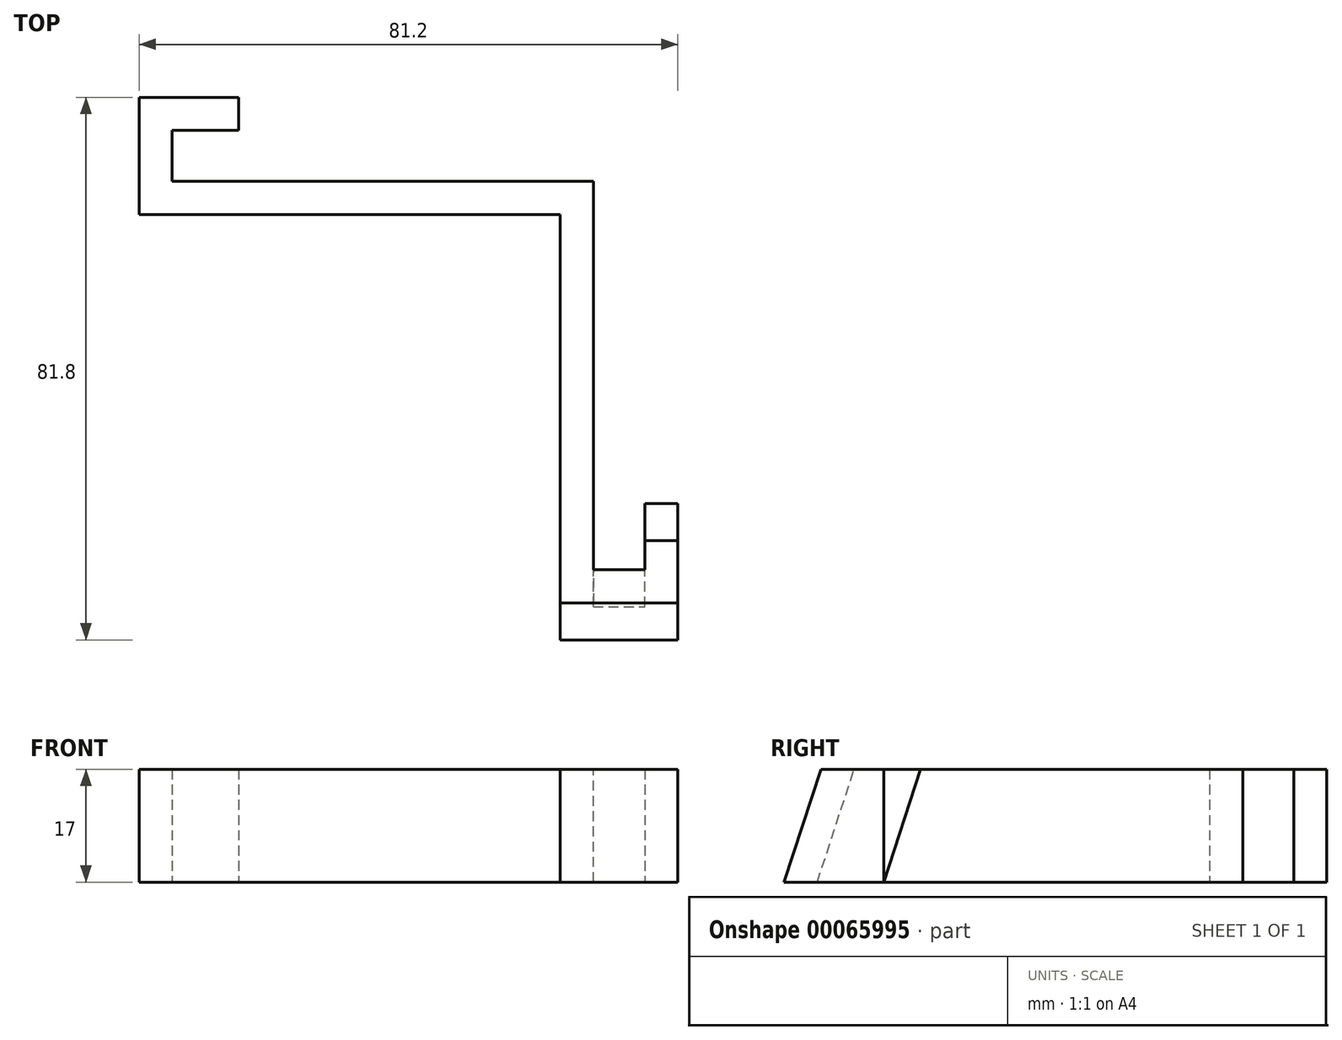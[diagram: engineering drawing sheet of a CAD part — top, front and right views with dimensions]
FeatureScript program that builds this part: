
annotation { "Feature Type Name" : "Feature", "Feature Type Description" : "" }
export const myFeature = defineFeature(function(context is Context, id is Id, definition is map)
    precondition{}
    {
        {
            var Q0;
            Q0=qCreatedBy(makeId("Top.planeOp"),FACE);
            var sketch = newSketch(context, id + "F0", { "sketchPlane" : qUnion([Q0])});
            skLineSegment(sketch, "E0", {"start": v(0, 0) * mm, "end": v(-63.45, 0) * mm});
            skLineSegment(sketch, "E1", {"start": v(0, 0) * mm, "end": v(0, -64.15) * mm});
            skLineSegment(sketch, "E2", {"start": v(0, -64.15) * mm, "end": v(7.75, -64.15) * mm});
            skLineSegment(sketch, "E3", {"start": v(-63.45, 0) * mm, "end": v(-63.45, 7.65) * mm});
            skLineSegment(sketch, "E4", {"start": v(7.75, -64.15) * mm, "end": v(7.75, -54.15) * mm});
            skLineSegment(sketch, "E5", {"start": v(7.75, -54.15) * mm, "end": v(12.75, -54.15) * mm});
            skLineSegment(sketch, "E6", {"start": v(-63.45, 7.65) * mm, "end": v(-53.45, 7.65) * mm});
            skLineSegment(sketch, "E7", {"start": v(-53.45, 7.65) * mm, "end": v(-53.45, 12.65) * mm});
            skLineSegment(sketch, "E8", {"start": v(12.75, -54.15) * mm, "end": v(12.75, -69.15) * mm});
            skLineSegment(sketch, "E9", {"start": v(12.75, -69.15) * mm, "end": v(-5, -69.15) * mm});
            skLineSegment(sketch, "E10", {"start": v(-5, -69.15) * mm, "end": v(-5, -5) * mm});
            skLineSegment(sketch, "E11", {"start": v(-5, -5) * mm, "end": v(-68.45, -5) * mm});
            skLineSegment(sketch, "E12", {"start": v(-68.45, -5) * mm, "end": v(-68.45, 12.65) * mm});
            skLineSegment(sketch, "E13", {"start": v(-68.45, 12.65) * mm, "end": v(-53.45, 12.65) * mm});
            skSolve(sketch);
        }
        {
            var Q0;
            Q0=makeQuery(id+"F0.imprint","IMPRINT",FACE,{"disambiguationData":[TD([[makeQuery(id+"F0.imprint","IMPRINT",EDGE,{"derivedFrom":sQuery(id+"F0.wireOp",EDGE,"E0")}),1.0]])]});
            extrude(context, id + "F1", {"entities" : qUnion([Q0]), "depth" : 17 * mm});
        }
        {
            var Q0;
            Q0=makeQuery(id+"F1.opExtrude","SWEPT_FACE",FACE,{"disambiguationData":[OSD([sQuery(id+"F0.wireOp",EDGE,"E1")])]});
            var sketch = newSketch(context, id + "F2", { "sketchPlane" : qUnion([Q0])});
            skLineSegment(sketch, "E14", {"start": v(-64.15, 17) * mm, "end": v(-58.58, 17) * mm});
            skLineSegment(sketch, "E15", {"start": v(-64.15, 0) * mm, "end": v(-58.58, 17) * mm});
            skLineSegment(sketch, "E16", {"start": v(-64.15, 17) * mm, "end": v(-64.15, 0) * mm});
            skSolve(sketch);
        }
        {
            var Q0;
            Q0=makeQuery(id+"F2.imprint","IMPRINT",FACE,{"disambiguationData":[TD([[makeQuery(id+"F2.imprint","IMPRINT",EDGE,{"derivedFrom":sQuery(id+"F2.wireOp",EDGE,"E14")}),1.0]])]});
            extrude(context, id + "F3", {"entities" : qUnion([Q0]), "operationType" : NewBodyOperationType.ADD, "depth" : 7.75 * mm});
        }
        {
            var Q0;
            Q0=makeQuery(id+"F1.opExtrude","SWEPT_FACE",FACE,{"disambiguationData":[OSD([sQuery(id+"F0.wireOp",EDGE,"E8")])]});
            var sketch = newSketch(context, id + "F4", { "sketchPlane" : qUnion([Q0])});
            skLineSegment(sketch, "E17", {"start": v(-54.15, 17) * mm, "end": v(-48.58, 17) * mm});
            skLineSegment(sketch, "E18", {"start": v(-48.58, 17) * mm, "end": v(-54.15, 0) * mm});
            skLineSegment(sketch, "E19", {"start": v(-54.15, 17) * mm, "end": v(-54.15, 0) * mm});
            skSolve(sketch);
        }
        {
            var Q0;
            Q0=makeQuery(id+"F4.imprint","IMPRINT",FACE,{"disambiguationData":[TD([[makeQuery(id+"F4.imprint","IMPRINT",EDGE,{"derivedFrom":sQuery(id+"F4.wireOp",EDGE,"E17")}),-1.0]])]});
            extrude(context, id + "F5", {"entities" : qUnion([Q0]), "oppositeDirection" : true, "depth" : 5 * mm});
        }
        {
            var Q0;
            Q0=makeQuery(id+"F1.opExtrude","SWEPT_FACE",FACE,{"disambiguationData":[OSD([sQuery(id+"F0.wireOp",EDGE,"E8")])]});
            var sketch = newSketch(context, id + "F6", { "sketchPlane" : qUnion([Q0])});
            skLineSegment(sketch, "E20", {"start": v(-69.15, 17) * mm, "end": v(-63.58, 17) * mm});
            skLineSegment(sketch, "E21", {"start": v(-63.58, 17) * mm, "end": v(-69.15, 0) * mm});
            skLineSegment(sketch, "E22", {"start": v(-69.15, 0) * mm, "end": v(-69.15, 17) * mm});
            skSolve(sketch);
        }
        {
            var Q0;
            Q0=makeQuery(id+"F6.imprint","IMPRINT",FACE,{"disambiguationData":[TD([[makeQuery(id+"F6.imprint","IMPRINT",EDGE,{"derivedFrom":sQuery(id+"F6.wireOp",EDGE,"E20")}),1.0]])]});
            extrude(context, id + "F7", {"entities" : qUnion([Q0]), "operationType" : NewBodyOperationType.REMOVE, "oppositeDirection" : true, "depth" : 25 * mm});
        }
    });
